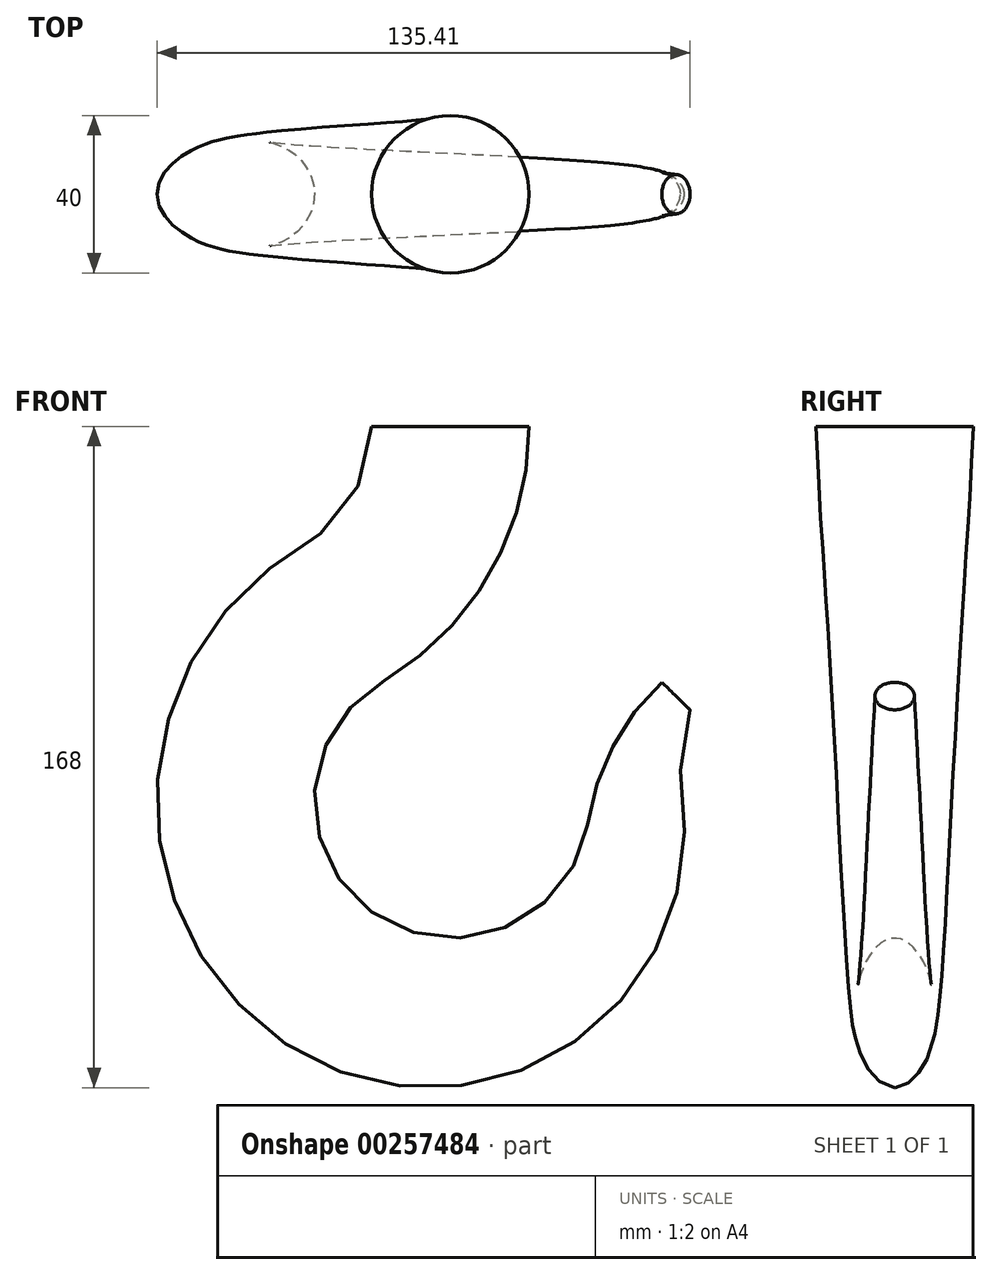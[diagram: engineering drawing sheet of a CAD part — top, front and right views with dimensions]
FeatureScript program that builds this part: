
annotation { "Feature Type Name" : "Feature", "Feature Type Description" : "" }
export const myFeature = defineFeature(function(context is Context, id is Id, definition is map)
    precondition{}
    {
        {
            var Q0;
            Q0=qCreatedBy(makeId("Front.planeOp"),FACE);
            var sketch = newSketch(context, id + "F0", { "sketchPlane" : qUnion([Q0])});
            skLineSegment(sketch, "E0", {"start": v(-20.45, 95) * mm, "end": v(19.55, 95) * mm});
            skArc(sketch, "E1", {"start": v(-20.45, 95) * mm, "mid": v(-25.1, 77.57) * mm, "end": v(-37.8, 64.77) * mm});
            skArc(sketch, "E2", {"start": v(19.55, 95) * mm, "mid": v(9.59, 57.65) * mm, "end": v(-17.64, 30.23) * mm});
            skArc(sketch, "E3", {"start": v(-17.64, 30.23) * mm, "mid": v(-19.64, -28.97) * mm, "end": v(34.61, -5.2) * mm});
            skArc(sketch, "E4", {"start": v(34.61, -5.2) * mm, "mid": v(40.94, 14) * mm, "end": v(53.27, 30) * mm});
            skLineSegment(sketch, "E5", {"start": v(53.27, 30) * mm, "end": v(60.41, 23) * mm});
            skArc(sketch, "E6", {"start": v(-37.8, 64.77) * mm, "mid": v(-74.88, 4.32) * mm, "end": v(-45, -60) * mm});
            skArc(sketch, "E7", {"start": v(-45, -60) * mm, "mid": v(26.93, -64.04) * mm, "end": v(58.4, 0.76) * mm});
            skArc(sketch, "E8", {"start": v(58.4, 0.76) * mm, "mid": v(58.15, 12) * mm, "end": v(60.41, 23) * mm});
            skCircle(sketch, "E9", {"center": v(56.84, 26.5) * mm, "radius": 5 * mm, "construction": true});
            skSolve(sketch);
        }
        {
            var Q0;
            Q0=sQuery(id+"F0.wireOp",EDGE,"E0");
            cPlane(context, id + "F1", {"entities" : qUnion([Q0]), "cplaneType" : CPlaneType.LINE_ANGLE, "offset" : 25 * mm, "angle" : 90 * degree, "width" : 150 * mm, "height" : 150 * mm});
        }
        {
            var Q0;
            Q0=qCreatedBy(id+"F1.planeOp",FACE);
            var sketch = newSketch(context, id + "F2", { "sketchPlane" : qUnion([Q0])});
            skLineSegment(sketch, "E10.0", {"start": v(-20.45, 0) * mm, "end": v(19.55, 0) * mm, "construction": true});
            skCircle(sketch, "E11", {"center": v(-0.45, 0) * mm, "radius": 20 * mm});
            skSolve(sketch);
        }
        {
            var Q0;
            Q0=sQuery(id+"F0.wireOp",EDGE,"E5");
            cPlane(context, id + "F3", {"entities" : qUnion([Q0]), "cplaneType" : CPlaneType.LINE_ANGLE, "offset" : 25 * mm, "angle" : 90 * degree, "width" : 150 * mm, "height" : 150 * mm});
        }
        {
            var Q0;
            Q0=qCreatedBy(id+"F3.planeOp",FACE);
            var sketch = newSketch(context, id + "F4", { "sketchPlane" : qUnion([Q0])});
            skLineSegment(sketch, "E12.0", {"start": v(17.04, 0) * mm, "end": v(27.04, 0) * mm, "construction": true});
            skCircle(sketch, "E13", {"center": v(22.04, 0) * mm, "radius": 5 * mm});
            skSolve(sketch);
        }
        {
            var Q0;
            Q0=qCreatedBy(makeId("Front.planeOp"),FACE);
            var sketch = newSketch(context, id + "F5", { "sketchPlane" : qUnion([Q0])});
            skArc(sketch, "E14.0", {"start": v(-20.45, 95) * mm, "mid": v(-25.1, 77.57) * mm, "end": v(-37.8, 64.77) * mm});
            skArc(sketch, "E15.0", {"start": v(-37.8, 64.77) * mm, "mid": v(-74.88, 4.32) * mm, "end": v(-45, -60) * mm});
            skArc(sketch, "E16.0", {"start": v(-45, -60) * mm, "mid": v(26.93, -64.04) * mm, "end": v(58.4, 0.76) * mm});
            skArc(sketch, "E17.0", {"start": v(58.4, 0.76) * mm, "mid": v(58.15, 12) * mm, "end": v(60.41, 23) * mm});
            skSolve(sketch);
        }
        {
            var Q0;
            Q0=qCreatedBy(makeId("Front.planeOp"),FACE);
            var sketch = newSketch(context, id + "F6", { "sketchPlane" : qUnion([Q0])});
            skArc(sketch, "E18.0", {"start": v(19.55, 95) * mm, "mid": v(9.59, 57.65) * mm, "end": v(-17.64, 30.23) * mm});
            skArc(sketch, "E19.0", {"start": v(-17.64, 30.23) * mm, "mid": v(-19.64, -28.97) * mm, "end": v(34.61, -5.2) * mm});
            skArc(sketch, "E20.0", {"start": v(34.61, -5.2) * mm, "mid": v(40.94, 14) * mm, "end": v(53.27, 30) * mm});
            skSolve(sketch);
        }
        {
            var Q0;
            Q0=makeQuery(id+"F2.imprint","IMPRINT",FACE,{"disambiguationData":[TD([[makeQuery(id+"F2.imprint","IMPRINT",EDGE,{"derivedFrom":sQuery(id+"F2.wireOp",EDGE,"E11")}),1.0]])]});
            var Q1;
            Q1=makeQuery(id+"F4.imprint","IMPRINT",FACE,{"disambiguationData":[TD([[makeQuery(id+"F4.imprint","IMPRINT",EDGE,{"derivedFrom":sQuery(id+"F4.wireOp",EDGE,"E13")}),1.0]])]});
            var Q2;
            Q2 = qConstructionFilter(qBodyType(qCreatedBy(id + "F5" ,EDGE), BodyType.WIRE), ConstructionObject.NO);
            var Q3;
            Q3 = qConstructionFilter(qBodyType(qCreatedBy(id + "F6" ,EDGE), BodyType.WIRE), ConstructionObject.NO);
            loft(context, id + "F7", {"addGuides" : true, "sheetProfilesArray" : [{ "sheetProfileEntities" : qUnion([Q0]) }, { "sheetProfileEntities" : qUnion([Q1]) }], "guidesArray" : [{ "guideEntities" : qUnion([Q2]), "guideDerivativeType" : LoftGuideDerivativeType.DEFAULT, "guideDerivativeMagnitude" : 1 }, { "guideEntities" : qUnion([Q3]), "guideDerivativeType" : LoftGuideDerivativeType.DEFAULT, "guideDerivativeMagnitude" : 1 }]});
        }
    });
